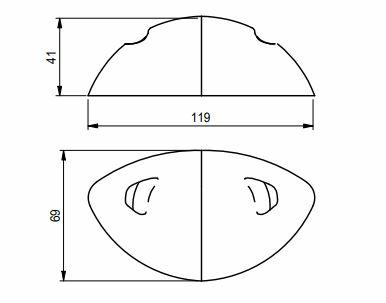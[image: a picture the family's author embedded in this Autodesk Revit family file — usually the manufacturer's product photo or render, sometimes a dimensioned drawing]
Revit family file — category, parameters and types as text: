
# Revit family: R-MBD-487
name_source: partatom
category: Portes
units: mm (PartAtom-declared; Revit-internal decimal feet)

## family parameters
Couper avec des vides une fois chargée = Non
Hôte = Mur
Partagée = Non
Repère de localisation dans la pièce = Oui
Toujours verticalement = Oui

## types (1)
- MBD-487
    1 Vantail = Non
    2 Vantaux = Oui
    A.E.V = non
    Acoustique = non
    Anti-Effraction = non
    Certification = D.A.S. Mode 2 certifié NF
    Code_MAJ = 2303130305MBD487
    Coloris_Chants = BER
    Coloris_Dormant = Hêtre
    Coloris_Face_Cote_Oppose_Ouverture = Prépeint
    Coloris_Face_Cote_Ouverture = Prépeint
    Construction analytique = <Aucun>
    DAS = Oui
    DC Larg Feuillure = 12 mm  [stored 0.0393701 ft]
    DC Pivot Vantail = 60 mm  [stored 0.19685 ft]
    Description = Bloc-porte bois D.A.S. 2 vantaux avec pivots linteaux motorisés encastrés, double action / va-et-vient, EI30, D.A.S. certifié NF, sur huisserie bois sans montant sans fileur
    Définir les propriétés thermiques par = Type schématique
    Ep Profil Pose Tunnel = 118 mm
    Ep Strat Vantail = 1 mm  [stored 0.00328084 ft]
    Ep Vantail = 51 mm  [stored 0.167323 ft]
    Epaisseur_Rainure à brique = 8 mm  [stored 0.0262467 ft]
    Fabricant = MALERBA
    Fiche_Produit = MBD-487
    Fileur = Non
    Hauteur_Tableau = 2125 mm
    Hauteur_Vantaux_Souhaitée = 2040 mm  [stored 6.69291 ft]
    Jeu_1 = 0 mm  [stored 0 ft]
    Jeu_2 = 0 mm  [stored 0 ft]
    Jeu_Côté_Articulation_Vantail = 8 mm  [stored 0.0262467 ft]
    Jeu_Côté_Fermeture_Vantail = 8 mm  [stored 0.0262467 ft]
    Jeu_Haut = 3 mm  [stored 0.00984252 ft]
    Larg Profil = 58 mm  [stored 0.190289 ft]
    Larg Profil Avec Fileur = 20 mm  [stored 0.0656168 ft]
    Larg Profil Trav = 76 mm  [stored 0.249344 ft]
    Largeur = 0 mm  [stored 0 ft]
    Largeur_Vantail_Semi_Fixe_Souhaitée = 930 mm  [stored 3.05118 ft]
    Largeur_Vantail_Service_Souhaitée = 930 mm  [stored 3.05118 ft]
    Mat APD = Caoutchouc noir
    Mat Parclose = BER 2
    Mat Parclose Métal = Peinture Laquée PMT - Blanc Pur - RAL 9010
    Materiaux_Dominant = Bois
    Modèle = Va et vient
    Montant_VV = Non
    Note d'identification = 2V EI30 DAS - LINTEAU MOTORISE - SANS MONTANT SANS FILEUR
    Pivot linteau motorisé = Oui
    Profondeur_Rainure à brique = 5 mm  [stored 0.0164042 ft]
    Reference_Commerciale = 2V/DA LINTEAU OP
    Resistance_Feu = EI30
    Sans_Montants = Oui
    Sens_Feu = Recto / Verso
    Thermique (W/m2.°K) = 0
    URL = https://www.malerba.fr
    X_Axe Pivot = 68 mm  [stored 0.223097 ft]
    X_DC seuil = 9 mm  [stored 0.0295276 ft]
    X_Inv_DC Larg Feuillure_1V Montant = 0 mm  [stored 0 ft]

note: [stored X ft] marks values corroborated as IEEE doubles in the binary element streams (Revit-internal decimal feet)

## geometry (parser evidence)
native form markers: Blend x14
no freeform markers — native parametric forms only
